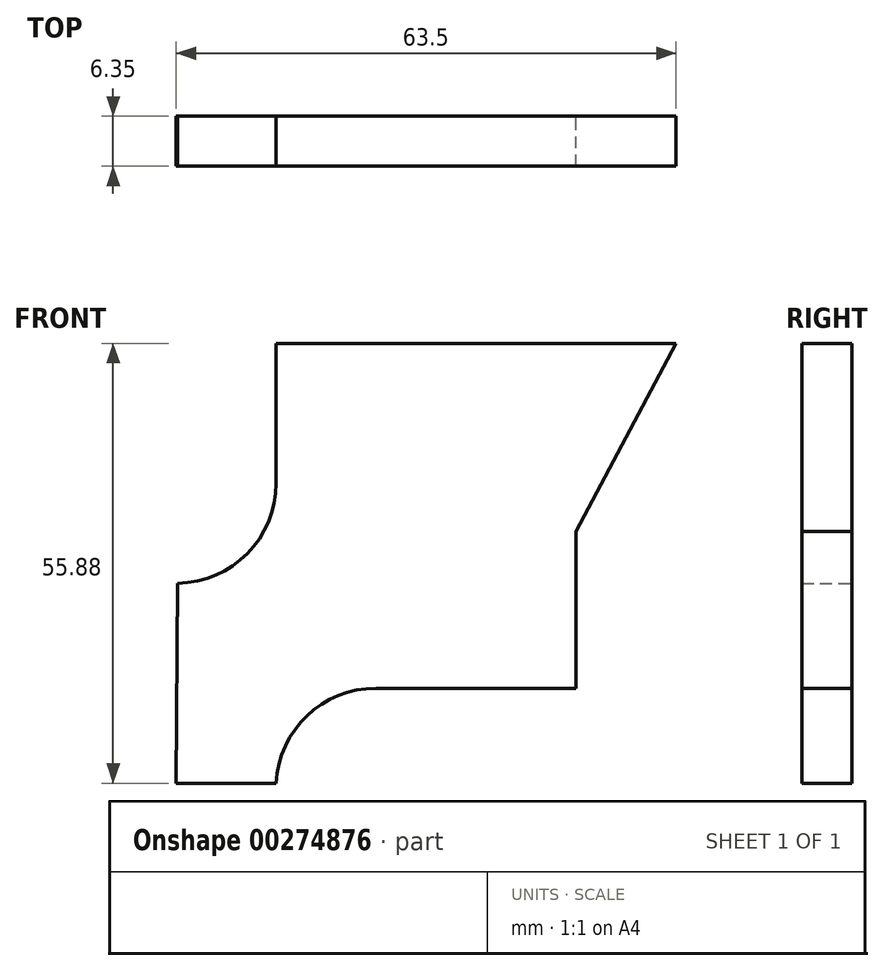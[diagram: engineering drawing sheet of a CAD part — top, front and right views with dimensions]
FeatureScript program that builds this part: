
annotation { "Feature Type Name" : "Feature", "Feature Type Description" : "" }
export const myFeature = defineFeature(function(context is Context, id is Id, definition is map)
    precondition{}
    {
        {
            var Q0;
            Q0=qCreatedBy(makeId("Front.planeOp"),FACE);
            var sketch = newSketch(context, id + "F0", { "sketchPlane" : qUnion([Q0])});
            skLineSegment(sketch, "E0", {"start": v(-39.27, -44.69) * mm, "end": v(-26.57, -44.69) * mm});
            skLineSegment(sketch, "E1", {"start": v(-13.89, -32.62) * mm, "end": v(11.53, -32.62) * mm});
            skLineSegment(sketch, "E2", {"start": v(11.53, -32.62) * mm, "end": v(11.53, -12.7) * mm});
            skLineSegment(sketch, "E3", {"start": v(11.53, -12.7) * mm, "end": v(24.23, 11.2) * mm});
            skLineSegment(sketch, "E4", {"start": v(24.23, 11.2) * mm, "end": v(-26.57, 11.2) * mm});
            skLineSegment(sketch, "E5", {"start": v(-26.57, 11.2) * mm, "end": v(-26.57, -6.59) * mm});
            skArc(sketch, "E6.filletArc", {"start": v(-13.89, -32.62) * mm, "mid": v(-22.64, -36.12) * mm, "end": v(-26.57, -44.69) * mm});
            skLineSegment(sketch, "E7", {"start": v(-39.12, -19.29) * mm, "end": v(-39.27, -44.69) * mm});
            skArc(sketch, "E8.filletArc", {"start": v(-39.12, -19.29) * mm, "mid": v(-30.24, -15.51) * mm, "end": v(-26.57, -6.59) * mm});
            skSolve(sketch);
        }
        {
            var Q0;
            Q0 = qSketchRegion(id + "F0", true);
            extrude(context, id + "F1", {"entities" : qUnion([Q0]), "depth" : 6.35 * mm});
        }
    });
